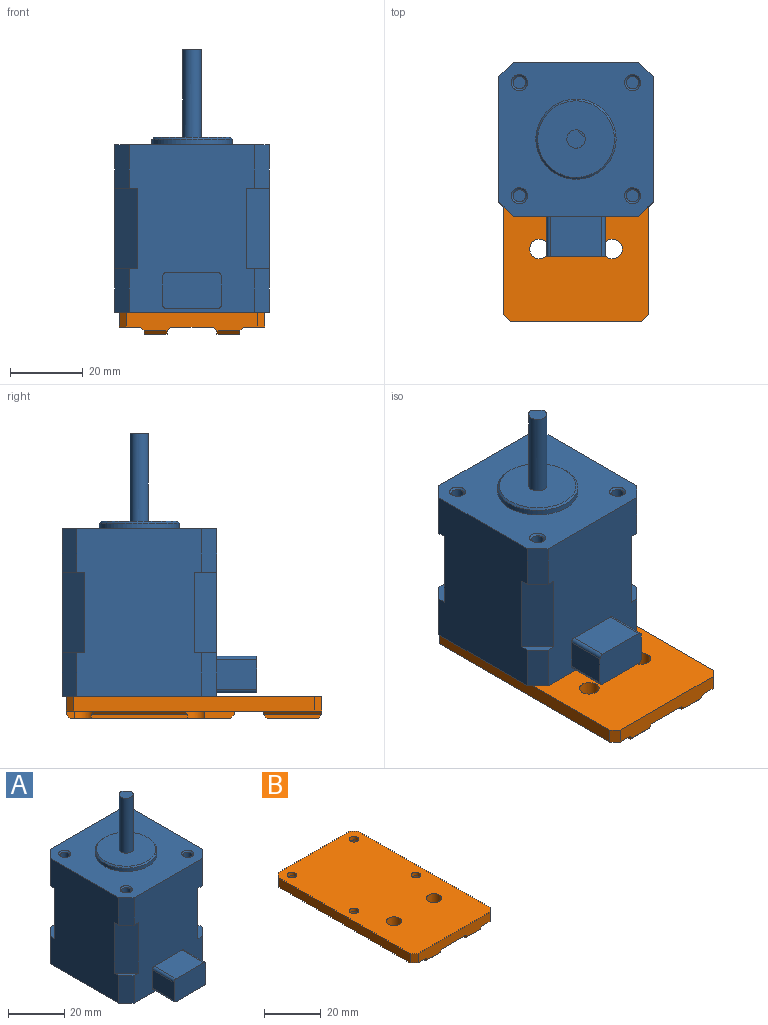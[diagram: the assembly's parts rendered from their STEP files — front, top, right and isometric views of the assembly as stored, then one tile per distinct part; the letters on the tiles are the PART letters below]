
ASSEMBLY  parts=2 mates=1
PART A: 66 faces, bbox 42.3x53.3x72 mm
  f0: plane 46x34.3mm, normal (0,-1,0), area 1325.3mm2, adj f1,f2,f5,f6,f12,f25,f26,f29
  f1: plane 6.12x6.12mm, normal (0,0,1), area 10.7mm2, adj f0,f4,f5,f25
  f2: plane 6.12x6.12mm, normal (0,0,1), area 10.7mm2, adj f0,f6,f7,f26
  f3: plane 6.12x6.12mm, normal (0,0,1), area 10.7mm2, adj f7,f8,f9,f27
  f4: plane 46x34.3mm, normal (-1,0,0), area 1484.5mm2, adj f1,f5,f10,f11,f12,f25,f28,f29
  f5: plane 12x4mm, normal (-0.71,-0.71,0), area 67.9mm2, adj f0,f1,f4,f12
  f6: plane 12x4mm, normal (0.71,-0.71,0), area 67.9mm2, adj f0,f2,f7,f12
  f7: plane 46x34.3mm, normal (1,0,0), area 1484.5mm2, adj f2,f3,f6,f8,f12,f26,f27,f30
  f8: plane 12x4mm, normal (0.71,0.71,0), area 67.9mm2, adj f3,f7,f9,f12
  f9: plane 46x34.3mm, normal (0,1,0), area 1484.5mm2, adj f3,f8,f10,f11,f12,f27,f28,f31
  f10: plane 12x4mm, normal (-0.71,0.71,0), area 67.9mm2, adj f4,f9,f11,f12
  f11: plane 6.12x6.12mm, normal (0,0,1), area 10.7mm2, adj f4,f9,f10,f28
  f12: plane 42.3x42.3mm, normal (0,0,-1), area 1696.5mm2, adj f0,f4,f5,f6,f7,f8,f9,f10
  f13: cylinder r=1.7mm len=7.5mm, axis (0,0,-1), area 80.1mm2, adj f14,f22
  f14: plane 3.4x3.4mm, normal (0,0,-1), area 9.1mm2, adj f13
  f15: cylinder r=1.7mm len=7.5mm, axis (0,0,-1), area 80.1mm2, adj f16,f24
  f16: plane 3.4x3.4mm, normal (0,0,-1), area 9.1mm2, adj f15
  f17: cylinder r=1.7mm len=7.5mm, axis (0,0,-1), area 80.1mm2, adj f18,f23
  f18: plane 3.4x3.4mm, normal (0,0,-1), area 9.1mm2, adj f17
  f19: cylinder r=1.7mm len=7.5mm, axis (0,0,-1), area 80.1mm2, adj f20,f21
  f20: plane 3.4x3.4mm, normal (0,0,-1), area 9.1mm2, adj f19
  f21: cone r=2.2mm half-angle=45deg, axis (0,0,-1), area 8.7mm2, adj f12,f19
  f22: cone r=2.2mm half-angle=45deg, axis (0,0,-1), area 8.7mm2, adj f12,f13
  f23: cone r=2.2mm half-angle=45deg, axis (0,0,-1), area 8.7mm2, adj f12,f17
  f24: cone r=2.2mm half-angle=45deg, axis (0,0,-1), area 8.7mm2, adj f12,f15
  f25: plane 22x6.12mm, normal (-0.71,-0.71,0), area 190.5mm2, adj f0,f1,f4,f29
  f26: plane 22x6.12mm, normal (0.71,-0.71,0), area 190.5mm2, adj f0,f2,f7,f30
  f27: plane 22x6.12mm, normal (0.71,0.71,0), area 190.5mm2, adj f3,f7,f9,f31
  f28: plane 22x6.12mm, normal (-0.71,0.71,0), area 190.5mm2, adj f4,f9,f11,f36
  f29: plane 6.12x6.12mm, normal (0,0,-1), area 10.7mm2, adj f0,f4,f25,f32
  f30: plane 6.12x6.12mm, normal (0,0,-1), area 10.7mm2, adj f0,f7,f26,f33
  f31: plane 6.12x6.12mm, normal (0,0,-1), area 10.7mm2, adj f7,f9,f27,f34
  f32: plane 12x4mm, normal (-0.71,-0.71,0), area 67.9mm2, adj f0,f4,f29,f37
  f33: plane 12x4mm, normal (0.71,-0.71,0), area 67.9mm2, adj f0,f7,f30,f37
  f34: plane 12x4mm, normal (0.71,0.71,0), area 67.9mm2, adj f7,f9,f31,f37
  f35: plane 12x4mm, normal (-0.71,0.71,0), area 67.9mm2, adj f4,f9,f36,f37
  f36: plane 6.12x6.12mm, normal (0,0,-1), area 10.7mm2, adj f4,f9,f28,f35
  f37: plane 42.3x42.3mm, normal (0,0,1), area 1316.3mm2, adj f0,f4,f7,f9,f32,f33,f34,f35
  f38: cylinder r=1.7mm len=7.5mm, axis (0,0,1), area 80.1mm2, adj f39,f49
  f39: plane 3.4x3.4mm, normal (0,0,1), area 9.1mm2, adj f38
  f40: cylinder r=1.7mm len=7.5mm, axis (0,0,1), area 80.1mm2, adj f41,f50
  f41: plane 3.4x3.4mm, normal (0,0,1), area 9.1mm2, adj f40
  f42: cylinder r=1.7mm len=7.5mm, axis (0,0,1), area 80.1mm2, adj f43,f51
  f43: plane 3.4x3.4mm, normal (0,0,1), area 9.1mm2, adj f42
  f44: cylinder r=1.7mm len=7.5mm, axis (0,0,1), area 80.1mm2, adj f45,f52
  f45: plane 3.4x3.4mm, normal (0,0,1), area 9.1mm2, adj f44
  f46: cylinder r=11mm len=22mm, axis (0,0,-1), area 103.7mm2, adj f37,f48
  f47: plane 21x21mm, normal (0,0,1), area 326.7mm2, adj f48,f54
  f48: cone r=10.5mm half-angle=45deg, axis (0,0,-1), area 47.8mm2, adj f46,f47
  f49: cone r=1.7mm half-angle=45deg, axis (0,0,1), area 8.7mm2, adj f37,f38
  f50: cone r=1.7mm half-angle=45deg, axis (0,0,1), area 8.7mm2, adj f37,f40
  f51: cone r=1.7mm half-angle=45deg, axis (0,0,1), area 8.7mm2, adj f37,f42
  f52: cone r=1.7mm half-angle=45deg, axis (0,0,1), area 8.7mm2, adj f37,f44
  f53: plane 2.12x2.12mm, normal (0,0,1), area 1mm2, adj f54,f55
  f54: cylinder r=2.5mm len=24mm, axis (0,0,-1), area 328.7mm2, adj f47,f53,f55,f56
  f55: plane 15x2.12mm, normal (0.71,0.71,0), area 45mm2, adj f53,f54,f56
  f56: plane 5x5mm, normal (0,0,1), area 18.6mm2, adj f54,f55
  f57: plane 11x8mm, normal (-1,0,0), area 88mm2, adj f0,f58,f62,f64
  f58: plane 16x10mm, normal (0,-1,0), area 159.1mm2, adj f57,f59,f60,f61,f62,f63,f64,f65
  f59: plane 11x8mm, normal (1,0,0), area 88mm2, adj f0,f58,f63,f65
  f60: plane 14x11mm, normal (0,0,1), area 154mm2, adj f0,f58,f64,f65
  f61: plane 14x11mm, normal (0,0,-1), area 154mm2, adj f0,f58,f62,f63
  f62: cylinder r=1mm len=11mm, axis (0,-1,0), area 17.3mm2, adj f0,f57,f58,f61
  f63: cylinder r=1mm len=11mm, axis (0,1,0), area 17.3mm2, adj f0,f58,f59,f61
  f64: cylinder r=1mm len=11mm, axis (0,1,0), area 17.3mm2, adj f0,f57,f58,f60
  f65: cylinder r=1mm len=11mm, axis (0,-1,0), area 17.3mm2, adj f0,f58,f59,f60
PART B: 60 faces, bbox 40x70x6 mm
  f0: plane 26.37x1mm, normal (-1,0,0), area 26.4mm2, adj f20,f36,f38,f58
  f1: plane 8.18x2mm, normal (-1,0,0), area 15.9mm2, adj f6,f18,f20,f38,f45
  f2: plane 2.18x2mm, normal (-1,0,0), area 3.9mm2, adj f6,f7,f20,f36,f51
  f3: plane 26.37x1mm, normal (1,0,0), area 26.4mm2, adj f31,f32,f34,f54
  f4: plane 8.18x2mm, normal (1,0,0), area 15.9mm2, adj f6,f30,f31,f34,f44
  f5: plane 2.18x2mm, normal (1,0,0), area 3.9mm2, adj f6,f7,f31,f32,f50
  f6: plane 70x40mm, normal (0,0,-1), area 1633.1mm2, adj f1,f2,f4,f5,f7,f8,f9,f10
  f7: plane 36x5mm, normal (0,1,0), area 157.6mm2, adj f2,f5,f6,f17,f40,f41,f50,f51
  f8: plane 66x4mm, normal (-1,0,0), area 264mm2, adj f6,f17,f40,f42
  f9: plane 36x5mm, normal (0,-1,0), area 158.6mm2, adj f6,f17,f42,f43,f48,f49,f52,f53
  f10: cylinder r=2.7mm len=5.4mm, axis (0,0,-1), area 67.9mm2, adj f6,f17
  f11: cylinder r=1.7mm len=3.4mm, axis (0,0,-1), area 16mm2, adj f17,f33
  f12: cylinder r=1.7mm len=3.4mm, axis (0,0,-1), area 16mm2, adj f17,f35
  f13: cylinder r=1.7mm len=3.4mm, axis (0,0,-1), area 16mm2, adj f17,f39
  f14: cylinder r=1.7mm len=3.4mm, axis (0,0,-1), area 16mm2, adj f17,f37
  f15: plane 66x4mm, normal (1,0,0), area 264mm2, adj f6,f17,f41,f43
  f16: cylinder r=2.7mm len=5.4mm, axis (0,0,-1), area 67.9mm2, adj f6,f17
  f17: plane 70x40mm, normal (0,0,1), area 2709.9mm2, adj f7,f8,f9,f10,f11,f12,f13,f14
  f18: plane 7.3x1mm, normal (0,-1,0), area 6.8mm2, adj f1,f6,f45,f59
  f19: plane 46x1mm, normal (1,0,0), area 45mm2, adj f20,f45,f51,f59
  f20: plane 44x6.3mm, normal (0,0,-1), area 271.1mm2, adj f0,f1,f2,f19,f36,f38,f45,f51
  f21: plane 16x1mm, normal (-1,0,0), area 15mm2, adj f24,f47,f49,f56
  f22: plane 16x1mm, normal (1,0,0), area 15mm2, adj f24,f47,f49,f57
  f23: plane 8.3x1mm, normal (0,1,0), area 7.3mm2, adj f6,f47,f56,f57
  f24: plane 14x6.3mm, normal (0,0,-1), area 88.2mm2, adj f21,f22,f47,f49
  f25: plane 16x1mm, normal (1,0,0), area 15mm2, adj f28,f46,f48,f52
  f26: plane 8.3x1mm, normal (0,1,0), area 7.3mm2, adj f6,f46,f52,f53
  f27: plane 16x1mm, normal (-1,0,0), area 15mm2, adj f28,f46,f48,f53
  f28: plane 14x6.3mm, normal (0,0,-1), area 88.2mm2, adj f25,f27,f46,f48
  f29: plane 46x1mm, normal (-1,0,0), area 45mm2, adj f31,f44,f50,f55
  f30: plane 7.3x1mm, normal (0,-1,0), area 6.8mm2, adj f4,f6,f44,f55
  f31: plane 44x6.3mm, normal (0,0,-1), area 271.1mm2, adj f3,f4,f5,f29,f32,f34,f44,f50
  f32: cylinder r=3.3mm len=6.6mm, axis (0,0,-1), area 62.7mm2, adj f3,f5,f6,f31,f33,f54
  f33: plane 6.6x6.6mm, normal (0,0,-1), area 25.1mm2, adj f11,f32
  f34: cylinder r=3.3mm len=6.6mm, axis (0,0,-1), area 62.7mm2, adj f3,f4,f6,f31,f35,f54
  f35: plane 6.6x6.6mm, normal (0,0,-1), area 25.1mm2, adj f12,f34
  f36: cylinder r=3.3mm len=6.6mm, axis (0,0,-1), area 62.7mm2, adj f0,f2,f6,f20,f37,f58
  f37: plane 6.6x6.6mm, normal (0,0,-1), area 25.1mm2, adj f14,f36
  f38: cylinder r=3.3mm len=6.6mm, axis (0,0,-1), area 62.7mm2, adj f0,f1,f6,f20,f39,f58
  f39: plane 6.6x6.6mm, normal (0,0,-1), area 25.1mm2, adj f13,f38
  f40: plane 4x2mm, normal (-0.71,0.71,0), area 11.3mm2, adj f6,f7,f8,f17
  f41: plane 4x2mm, normal (0.71,0.71,0), area 11.3mm2, adj f6,f7,f15,f17
  f42: plane 4x2mm, normal (-0.71,-0.71,0), area 11.3mm2, adj f6,f8,f9,f17
  f43: plane 4x2mm, normal (0.71,-0.71,0), area 11.3mm2, adj f6,f9,f15,f17
  f44: plane 6.3x1mm, normal (0,-0.71,-0.71), area 8.9mm2, adj f4,f29,f30,f31
  f45: plane 6.3x1mm, normal (0,-0.71,-0.71), area 8.9mm2, adj f1,f18,f19,f20
  f46: plane 6.3x1mm, normal (0,0.71,-0.71), area 8.9mm2, adj f25,f26,f27,f28
  f47: plane 6.3x1mm, normal (0,0.71,-0.71), area 8.9mm2, adj f21,f22,f23,f24
  f48: plane 6.3x1mm, normal (0,-0.71,-0.71), area 8.9mm2, adj f9,f25,f27,f28
  f49: plane 6.3x1mm, normal (0,-0.71,-0.71), area 8.9mm2, adj f9,f21,f22,f24
  f50: plane 6.3x1mm, normal (0,0.71,-0.71), area 8.9mm2, adj f5,f7,f29,f31
  f51: plane 6.3x1mm, normal (0,0.71,-0.71), area 8.9mm2, adj f2,f7,f19,f20
  f52: plane 16x1mm, normal (0.71,0,-0.71), area 22.6mm2, adj f6,f9,f25,f26
  f53: plane 16x1mm, normal (-0.71,0,-0.71), area 22.6mm2, adj f6,f9,f26,f27
  f54: plane 26.37x1mm, normal (0.71,0,-0.71), area 36.2mm2, adj f3,f6,f32,f34
  f55: plane 46x1mm, normal (-0.71,0,-0.71), area 65.1mm2, adj f6,f7,f29,f30
  f56: plane 16x1mm, normal (-0.71,0,-0.71), area 22.6mm2, adj f6,f9,f21,f23
  f57: plane 16x1mm, normal (0.71,0,-0.71), area 22.6mm2, adj f6,f9,f22,f23
  f58: plane 26.37x1mm, normal (-0.71,0,-0.71), area 36.2mm2, adj f0,f6,f36,f38
  f59: plane 46x1mm, normal (0.71,0,-0.71), area 65.1mm2, adj f6,f7,f18,f19
PLACE A t=(0,0,4)mm
PLACE B at identity fixed
MATE fastened A.f13 <-> B.f14  axis (0,0,-1) through (-15.5,15.5,4)mm
